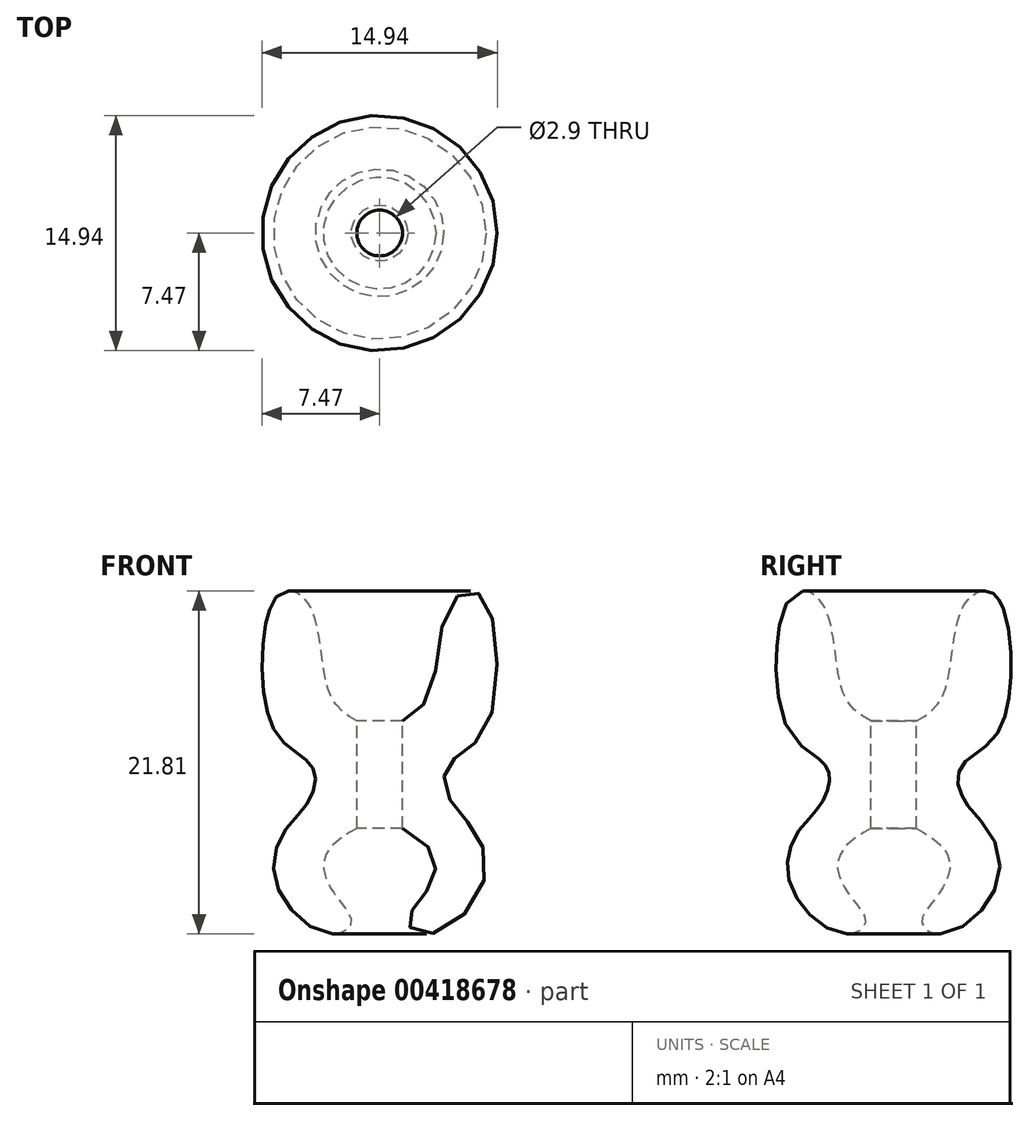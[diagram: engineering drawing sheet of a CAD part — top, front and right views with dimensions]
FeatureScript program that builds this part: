
annotation { "Feature Type Name" : "Feature", "Feature Type Description" : "" }
export const myFeature = defineFeature(function(context is Context, id is Id, definition is map)
    precondition{}
    {
        {
            var Q0;
            Q0=qCreatedBy(makeId("Front.planeOp"),FACE);
            var sketch = newSketch(context, id + "F0", { "sketchPlane" : qUnion([Q0])});
            skFitSpline(sketch, "E0", {"points": [v(1.45, 3.45) * mm, v(3.18, 5.17) * mm, v(4.35, 10.61) * mm, v(5.99, 11.7) * mm, v(7.26, 9.53) * mm, v(6.71, 2.9) * mm, v(4.9, 1.18) * mm, v(4.08, 0) * mm, v(4.63, -1.81) * mm, v(6.26, -3.9) * mm, v(6.44, -7.26) * mm, v(3.18, -10.07) * mm, v(1.81, -9.44) * mm, v(2.18, -8.44) * mm, v(3.27, -6.87) * mm, v(3.47, -5.17) * mm, v(1.45, -3.36) * mm], "startDerivative": vector(33.69, 19.84) * mm, "endDerivative": vector(-45.84, 25.36) * mm});
            skLineSegment(sketch, "E1", {"start": v(1.45, 3.45) * mm, "end": v(1.45, 0) * mm});
            skLineSegment(sketch, "E2", {"start": v(1.45, 0) * mm, "end": v(1.45, -3.36) * mm});
            skLineSegment(sketch, "E3", {"start": v(0, 6.24) * mm, "end": v(0, 3.83) * mm});
            skSolve(sketch);
        }
        {
            var Q0;
            Q0 = qSketchRegion(id + "F0", true);
            var Q1;
            Q1=sQuery(id+"F0.wireOp",EDGE,"E3");
            revolve(context, id + "F1", {"surfaceOperationType" : NewSurfaceOperationType.NEW, "entities" : qUnion([Q0]), "axis" : qUnion([Q1]), "revolveType" : RevolveType.FULL});
        }
    });
